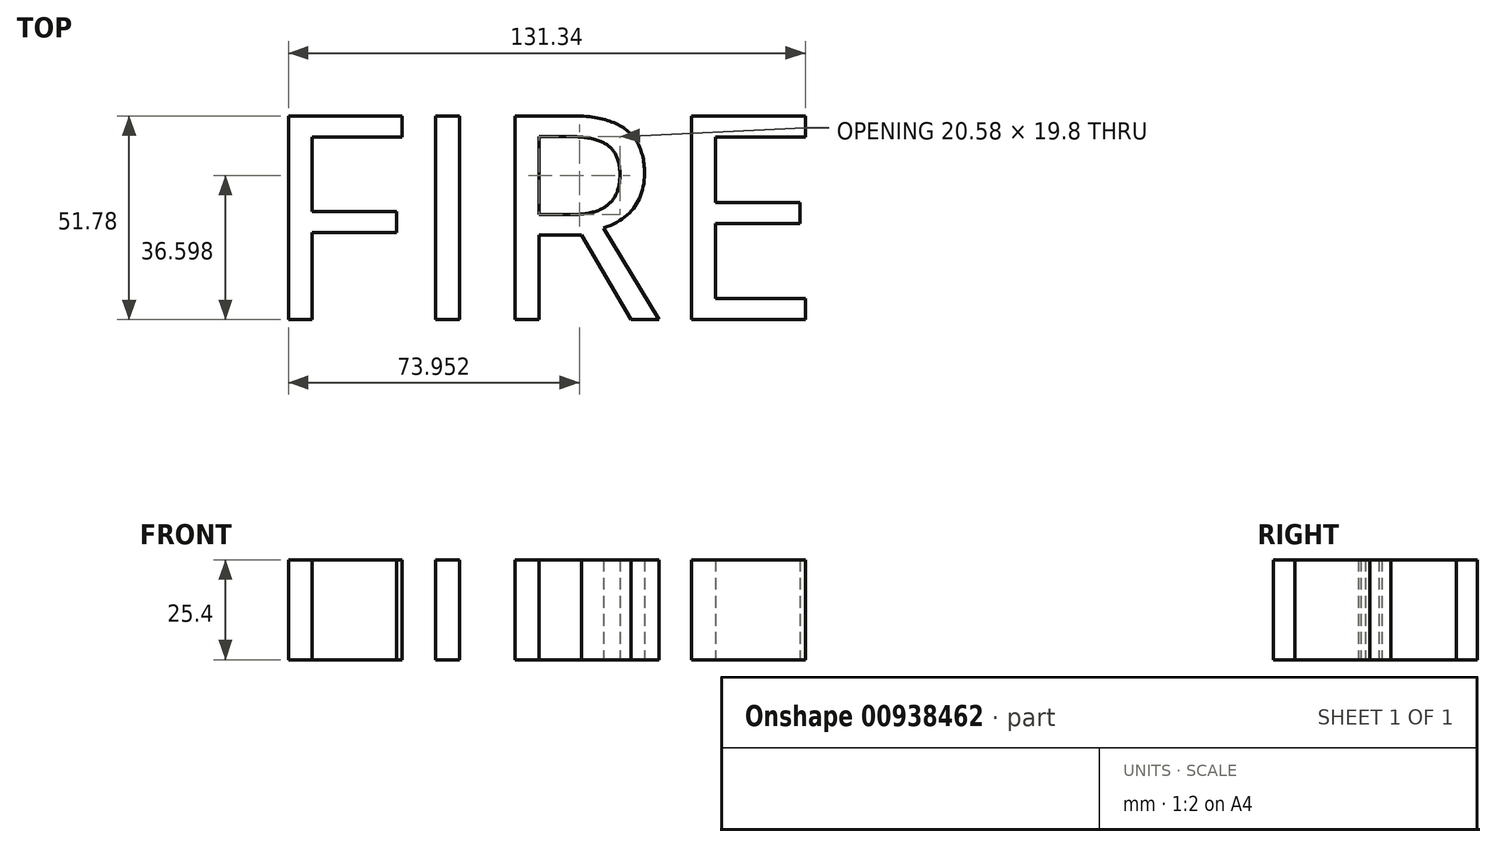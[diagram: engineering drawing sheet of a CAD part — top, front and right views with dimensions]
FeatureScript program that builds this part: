
annotation { "Feature Type Name" : "Feature", "Feature Type Description" : "" }
export const myFeature = defineFeature(function(context is Context, id is Id, definition is map)
    precondition{}
    {
        {
            var Q0;
            Q0=qCreatedBy(makeId("Top.planeOp"),FACE);
            var sketch = newSketch(context, id + "F0", { "sketchPlane" : qUnion([Q0])});
            skText(sketch, "E0", { "text": "FIRE", "fontName": "OpenSans-Regular.ttf"});
            const initialGuessF0  = {"E0": [-0.11326, -0.03573, 1, 0, 0.05222]};
            skSetInitialGuess(sketch, initialGuessF0);
            skSolve(sketch);
        }
        {
            var Q0;
            Q0 = qSketchRegion(id + "F0", true);
            extrude(context, id + "F1", {"entities" : qUnion([Q0]), "depth" : 25.4 * mm, "offsetDistance" : 25.4 * mm});
        }
    });
